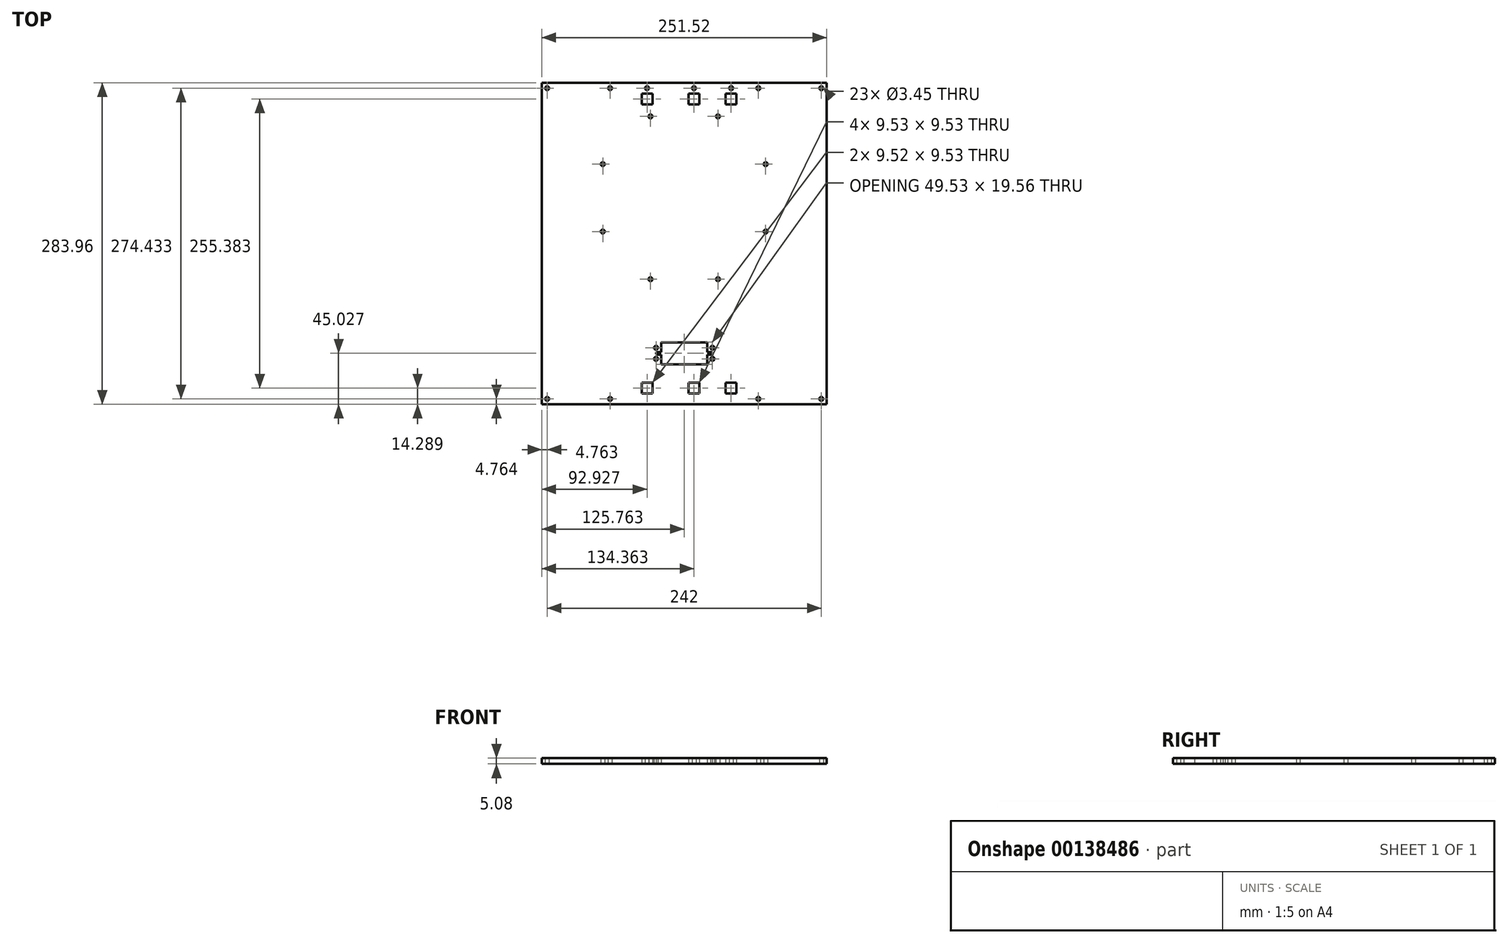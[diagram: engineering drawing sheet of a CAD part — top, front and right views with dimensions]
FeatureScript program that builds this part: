
annotation { "Feature Type Name" : "Feature", "Feature Type Description" : "" }
export const myFeature = defineFeature(function(context is Context, id is Id, definition is map)
    precondition{}
    {
        {
            var Q0;
            Q0=qCreatedBy(makeId("Top.planeOp"),FACE);
            var sketch = newSketch(context, id + "F0", { "sketchPlane" : qUnion([Q0])});
            skLineSegment(sketch, "E0.bottom", {"start": v(0, 0) * mm, "end": v(251.52, 0) * mm});
            skLineSegment(sketch, "E0.top", {"start": v(0, -283.96) * mm, "end": v(251.52, -283.96) * mm});
            skLineSegment(sketch, "E0.left", {"start": v(0, 0) * mm, "end": v(0, -283.96) * mm});
            skLineSegment(sketch, "E0.right", {"start": v(251.52, 0) * mm, "end": v(251.52, -283.96) * mm});
            skLineSegment(sketch, "E1", {"start": v(4.76, 0) * mm, "end": v(4.76, -4.76) * mm, "construction": true});
            skLineSegment(sketch, "E2", {"start": v(4.76, -4.76) * mm, "end": v(0, -4.76) * mm, "construction": true});
            skLineSegment(sketch, "E3", {"start": v(4.76, -4.76) * mm, "end": v(60.33, -4.76) * mm, "construction": true});
            skCircle(sketch, "E4", {"center": v(4.76, -4.76) * mm, "radius": 1.73 * mm});
            skCircle(sketch, "E5", {"center": v(60.33, -4.76) * mm, "radius": 1.73 * mm});
            skLineSegment(sketch, "E6", {"start": v(251.52, -4.76) * mm, "end": v(246.76, -4.76) * mm, "construction": true});
            skLineSegment(sketch, "E7", {"start": v(246.76, -4.76) * mm, "end": v(191.2, -4.76) * mm, "construction": true});
            skLineSegment(sketch, "E8", {"start": v(191.2, -4.76) * mm, "end": v(176.6, -4.76) * mm, "construction": true});
            skCircle(sketch, "E9", {"center": v(191.2, -4.76) * mm, "radius": 1.73 * mm});
            skCircle(sketch, "E10", {"center": v(246.76, -4.76) * mm, "radius": 1.73 * mm});
            skLineSegment(sketch, "E11", {"start": v(4.76, -283.96) * mm, "end": v(4.76, -279.2) * mm, "construction": true});
            skLineSegment(sketch, "E12", {"start": v(4.76, -279.2) * mm, "end": v(60.33, -279.2) * mm, "construction": true});
            skLineSegment(sketch, "E13", {"start": v(191.2, -279.2) * mm, "end": v(246.76, -279.2) * mm, "construction": true});
            skLineSegment(sketch, "E14", {"start": v(246.76, -279.2) * mm, "end": v(251.52, -279.2) * mm, "construction": true});
            skCircle(sketch, "E15", {"center": v(4.76, -279.2) * mm, "radius": 1.73 * mm});
            skCircle(sketch, "E16", {"center": v(60.33, -279.2) * mm, "radius": 1.73 * mm});
            skCircle(sketch, "E17", {"center": v(191.2, -279.2) * mm, "radius": 1.73 * mm});
            skCircle(sketch, "E18", {"center": v(246.76, -279.2) * mm, "radius": 1.73 * mm});
            skLineSegment(sketch, "E19", {"start": v(60.33, -4.76) * mm, "end": v(92.93, -4.76) * mm, "construction": true});
            skLineSegment(sketch, "E20", {"start": v(176.6, -4.76) * mm, "end": v(157.8, -4.76) * mm, "construction": true});
            skLineSegment(sketch, "E21", {"start": v(92.93, -4.76) * mm, "end": v(157.8, -4.76) * mm, "construction": true});
            skCircle(sketch, "E22", {"center": v(92.93, -4.76) * mm, "radius": 1.73 * mm});
            skCircle(sketch, "E23", {"center": v(134.36, -4.76) * mm, "radius": 1.73 * mm});
            skCircle(sketch, "E24", {"center": v(167.2, -4.76) * mm, "radius": 1.73 * mm});
            skLineSegment(sketch, "E25", {"start": v(92.93, -4.76) * mm, "end": v(92.93, -9.53) * mm, "construction": true});
            skLineSegment(sketch, "E26", {"start": v(134.36, -4.76) * mm, "end": v(134.36, -9.52) * mm, "construction": true});
            skLineSegment(sketch, "E27", {"start": v(167.2, -4.76) * mm, "end": v(167.2, -9.52) * mm, "construction": true});
            skLineSegment(sketch, "E28.bottom", {"start": v(88.17, -9.53) * mm, "end": v(97.7, -9.53) * mm});
            skLineSegment(sketch, "E28.top", {"start": v(88.17, -19.05) * mm, "end": v(97.7, -19.05) * mm});
            skLineSegment(sketch, "E28.left", {"start": v(88.17, -9.53) * mm, "end": v(88.17, -19.05) * mm});
            skLineSegment(sketch, "E28.right", {"start": v(97.7, -9.53) * mm, "end": v(97.7, -19.05) * mm});
            skLineSegment(sketch, "E29.bottom", {"start": v(129.6, -9.52) * mm, "end": v(139.12, -9.52) * mm});
            skLineSegment(sketch, "E29.top", {"start": v(129.6, -19.05) * mm, "end": v(139.12, -19.05) * mm});
            skLineSegment(sketch, "E29.left", {"start": v(129.6, -9.52) * mm, "end": v(129.6, -19.05) * mm});
            skLineSegment(sketch, "E29.right", {"start": v(139.12, -9.52) * mm, "end": v(139.12, -19.05) * mm});
            skLineSegment(sketch, "E30.bottom", {"start": v(162.43, -9.52) * mm, "end": v(171.96, -9.52) * mm});
            skLineSegment(sketch, "E30.top", {"start": v(162.43, -19.05) * mm, "end": v(171.96, -19.05) * mm});
            skLineSegment(sketch, "E30.left", {"start": v(162.43, -9.52) * mm, "end": v(162.43, -19.05) * mm});
            skLineSegment(sketch, "E30.right", {"start": v(171.96, -9.52) * mm, "end": v(171.96, -19.05) * mm});
            skLineSegment(sketch, "E31", {"start": v(125.76, 0) * mm, "end": v(125.76, -101.63) * mm, "construction": true});
            skCircle(sketch, "E32", {"center": v(125.76, -101.63) * mm, "radius": 82.58 * mm, "construction": true});
            skCircle(sketch, "E33", {"center": v(155.54, -29.74) * mm, "radius": 4.76 * mm, "construction": true});
            skCircle(sketch, "E34", {"center": v(155.54, -29.74) * mm, "radius": 1.73 * mm});
            skLineSegment(sketch, "E35", {"start": v(125.76, -101.63) * mm, "end": v(125.76, -184.21) * mm, "construction": true});
            skLineSegment(sketch, "E36", {"start": v(125.76, -184.21) * mm, "end": v(125.76, -238.93) * mm, "construction": true});
            skLineSegment(sketch, "E37.bottom", {"start": v(146.08, -229.15) * mm, "end": v(105.44, -229.15) * mm});
            skLineSegment(sketch, "E37.top", {"start": v(146.08, -248.71) * mm, "end": v(105.44, -248.71) * mm});
            skPoint(sketch, "E37.middle", {"position": v(125.76, -238.93) * mm});
            skLineSegment(sketch, "E38", {"start": v(146.08, -238.93) * mm, "end": v(136.66, -238.93) * mm, "construction": true});
            skLineSegment(sketch, "E39", {"start": v(136.66, -238.93) * mm, "end": v(125.76, -101.63) * mm, "construction": true});
            skLineSegment(sketch, "E40", {"start": v(125.76, -248.71) * mm, "end": v(125.76, -283.96) * mm, "construction": true});
            skLineSegment(sketch, "E41", {"start": v(60.33, -279.2) * mm, "end": v(92.93, -279.2) * mm, "construction": true});
            skLineSegment(sketch, "E42", {"start": v(92.93, -279.2) * mm, "end": v(92.93, -274.43) * mm, "construction": true});
            skLineSegment(sketch, "E43", {"start": v(191.2, -279.2) * mm, "end": v(167.2, -279.2) * mm, "construction": true});
            skLineSegment(sketch, "E44", {"start": v(167.2, -279.2) * mm, "end": v(167.2, -274.43) * mm, "construction": true});
            skLineSegment(sketch, "E45.bottom", {"start": v(88.17, -274.43) * mm, "end": v(97.7, -274.43) * mm});
            skLineSegment(sketch, "E45.top", {"start": v(88.17, -264.9) * mm, "end": v(97.7, -264.9) * mm});
            skLineSegment(sketch, "E45.left", {"start": v(88.17, -274.43) * mm, "end": v(88.17, -264.9) * mm});
            skLineSegment(sketch, "E45.right", {"start": v(97.7, -274.43) * mm, "end": v(97.7, -264.9) * mm});
            skLineSegment(sketch, "E46.bottom", {"start": v(162.43, -274.43) * mm, "end": v(171.96, -274.43) * mm});
            skLineSegment(sketch, "E46.top", {"start": v(162.43, -264.9) * mm, "end": v(171.96, -264.9) * mm});
            skLineSegment(sketch, "E46.left", {"start": v(162.43, -274.43) * mm, "end": v(162.43, -264.9) * mm});
            skLineSegment(sketch, "E46.right", {"start": v(171.96, -274.43) * mm, "end": v(171.96, -264.9) * mm});
            skLineSegment(sketch, "E47", {"start": v(92.93, -279.2) * mm, "end": v(134.36, -279.2) * mm, "construction": true});
            skLineSegment(sketch, "E48", {"start": v(134.36, -279.2) * mm, "end": v(167.2, -279.2) * mm, "construction": true});
            skLineSegment(sketch, "E49", {"start": v(134.36, -279.2) * mm, "end": v(134.36, -274.43) * mm, "construction": true});
            skLineSegment(sketch, "E50.bottom", {"start": v(129.6, -274.43) * mm, "end": v(139.12, -274.43) * mm});
            skLineSegment(sketch, "E50.top", {"start": v(129.6, -264.9) * mm, "end": v(139.12, -264.9) * mm});
            skLineSegment(sketch, "E50.left", {"start": v(129.6, -274.43) * mm, "end": v(129.6, -264.9) * mm});
            skLineSegment(sketch, "E50.right", {"start": v(139.12, -274.43) * mm, "end": v(139.12, -264.9) * mm});
            skCircle(sketch, "E51.cCircle", {"center": v(125.76, -101.63) * mm, "radius": 71.9 * mm, "construction": true});
            skLineSegment(sketch, "E51.0", {"start": v(155.54, -29.74) * mm, "end": v(197.66, -71.85) * mm, "construction": true});
            skLineSegment(sketch, "E51.1", {"start": v(197.66, -71.85) * mm, "end": v(197.66, -131.41) * mm, "construction": true});
            skLineSegment(sketch, "E51.2", {"start": v(197.66, -131.41) * mm, "end": v(155.54, -173.53) * mm, "construction": true});
            skLineSegment(sketch, "E51.3", {"start": v(155.54, -173.53) * mm, "end": v(95.98, -173.53) * mm, "construction": true});
            skLineSegment(sketch, "E51.4", {"start": v(95.98, -173.53) * mm, "end": v(53.87, -131.41) * mm, "construction": true});
            skLineSegment(sketch, "E51.5", {"start": v(53.87, -131.41) * mm, "end": v(53.87, -71.85) * mm, "construction": true});
            skLineSegment(sketch, "E51.6", {"start": v(53.87, -71.85) * mm, "end": v(95.98, -29.74) * mm, "construction": true});
            skLineSegment(sketch, "E51.7", {"start": v(95.98, -29.74) * mm, "end": v(155.54, -29.74) * mm, "construction": true});
            skPoint(sketch, "E51.0.midPoint", {"position": v(176.6, -50.8) * mm});
            skCircle(sketch, "E52", {"center": v(53.87, -71.85) * mm, "radius": 1.73 * mm});
            skCircle(sketch, "E53", {"center": v(95.98, -29.74) * mm, "radius": 1.73 * mm});
            skCircle(sketch, "E54", {"center": v(53.87, -131.41) * mm, "radius": 1.73 * mm});
            skCircle(sketch, "E55", {"center": v(95.98, -173.53) * mm, "radius": 1.73 * mm});
            skCircle(sketch, "E56", {"center": v(155.54, -173.53) * mm, "radius": 1.73 * mm});
            skCircle(sketch, "E57", {"center": v(197.66, -131.41) * mm, "radius": 1.73 * mm});
            skCircle(sketch, "E58", {"center": v(197.66, -71.85) * mm, "radius": 1.73 * mm});
            skLineSegment(sketch, "E59.bottom", {"start": v(146.08, -237.92) * mm, "end": v(149.51, -237.92) * mm});
            skLineSegment(sketch, "E59.top", {"start": v(146.08, -239.95) * mm, "end": v(149.51, -239.95) * mm});
            skLineSegment(sketch, "E59.left", {"start": v(146.08, -237.92) * mm, "end": v(146.08, -239.95) * mm, "construction": true});
            skLineSegment(sketch, "E59.right", {"start": v(149.51, -237.92) * mm, "end": v(149.51, -239.95) * mm, "construction": true});
            skLineSegment(sketch, "E60", {"start": v(146.08, -237.92) * mm, "end": v(146.08, -229.15) * mm});
            skLineSegment(sketch, "E61", {"start": v(146.08, -239.95) * mm, "end": v(146.08, -248.71) * mm});
            skArc(sketch, "E62", {"start": v(149.51, -239.95) * mm, "mid": v(150.53, -238.93) * mm, "end": v(149.51, -237.92) * mm});
            skLineSegment(sketch, "E63.bottom", {"start": v(105.44, -239.95) * mm, "end": v(102.01, -239.95) * mm});
            skLineSegment(sketch, "E63.top", {"start": v(105.44, -237.92) * mm, "end": v(102.01, -237.92) * mm});
            skLineSegment(sketch, "E63.left", {"start": v(105.44, -239.95) * mm, "end": v(105.44, -237.92) * mm, "construction": true});
            skLineSegment(sketch, "E63.right", {"start": v(102.01, -239.95) * mm, "end": v(102.01, -237.92) * mm, "construction": true});
            skLineSegment(sketch, "E64", {"start": v(105.44, -229.15) * mm, "end": v(105.44, -237.92) * mm});
            skLineSegment(sketch, "E65", {"start": v(105.44, -239.95) * mm, "end": v(105.44, -248.71) * mm});
            skArc(sketch, "E66", {"start": v(102.01, -237.92) * mm, "mid": v(101, -238.93) * mm, "end": v(102.01, -239.95) * mm});
            skLineSegment(sketch, "E67.bottom", {"start": v(150.65, -243.82) * mm, "end": v(100.87, -243.82) * mm, "construction": true});
            skLineSegment(sketch, "E67.top", {"start": v(150.65, -234.04) * mm, "end": v(100.87, -234.04) * mm, "construction": true});
            skLineSegment(sketch, "E67.left", {"start": v(150.65, -243.82) * mm, "end": v(150.65, -234.04) * mm, "construction": true});
            skLineSegment(sketch, "E67.right", {"start": v(100.87, -243.82) * mm, "end": v(100.87, -234.04) * mm, "construction": true});
            skCircle(sketch, "E68", {"center": v(150.65, -234.04) * mm, "radius": 1.73 * mm});
            skCircle(sketch, "E69", {"center": v(150.65, -243.82) * mm, "radius": 1.73 * mm});
            skCircle(sketch, "E70", {"center": v(100.87, -243.82) * mm, "radius": 1.73 * mm});
            skCircle(sketch, "E71", {"center": v(100.87, -234.04) * mm, "radius": 1.73 * mm});
            skSolve(sketch);
        }
        {
            var Q0;
            Q0=qSketchRegion(id+"F0",true);
            extrude(context, id + "F1", {"entities" : qUnion([Q0]), "depth" : 5.08 * mm});
        }
    });
